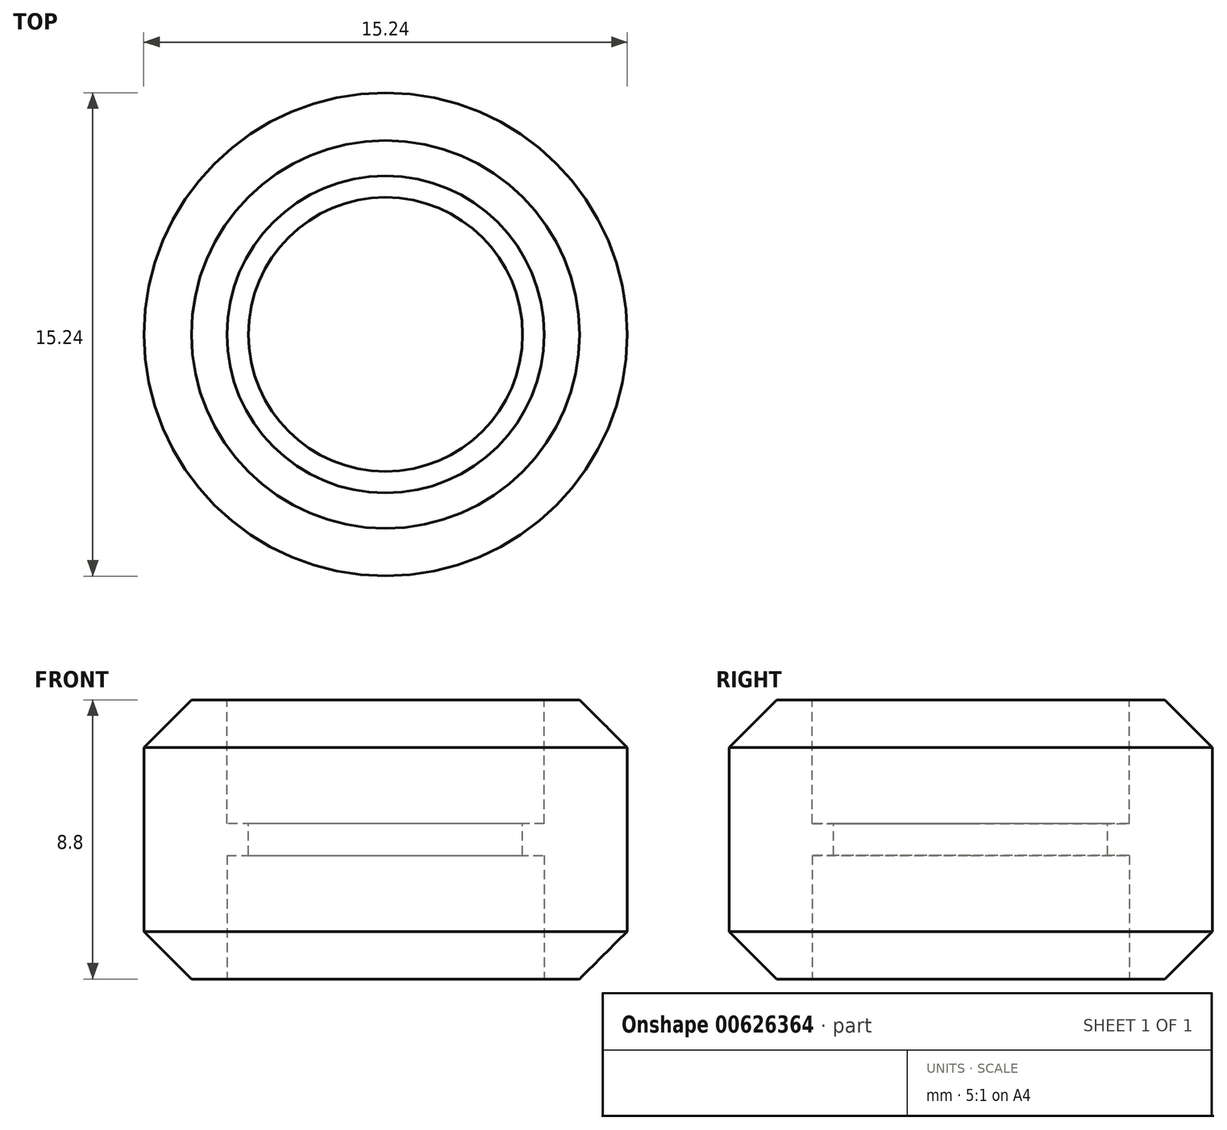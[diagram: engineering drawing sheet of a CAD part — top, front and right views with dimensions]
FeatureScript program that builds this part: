
annotation { "Feature Type Name" : "Feature", "Feature Type Description" : "" }
export const myFeature = defineFeature(function(context is Context, id is Id, definition is map)
    precondition{}
    {
        {
            var Q0;
            Q0=qCreatedBy(makeId("Top.planeOp"),FACE);
            var sketch = newSketch(context, id + "F0", { "sketchPlane" : qUnion([Q0])});
            skCircle(sketch, "E0", {"center": v(0, 0) * mm, "radius": 7.62 * mm});
            skSolve(sketch);
        }
        {
            var Q0;
            Q0 = qSketchRegion(id + "F0", true);
            extrude(context, id + "F1", {"entities" : qUnion([Q0]), "depth" : 8.8 * mm, "offsetDistance" : 25 * mm});
        }
        {
            var Q0;
            Q0=makeQuery(id+"F1.opExtrude","CAP_EDGE",EDGE,{"disambiguationData":[OSD([sQuery(id+"F0.wireOp",EDGE,"E0")])],"isStart":false});
            var Q1;
            Q1=makeQuery(id+"F1.opExtrude","CAP_EDGE",EDGE,{"disambiguationData":[OSD([sQuery(id+"F0.wireOp",EDGE,"E0")])],"isStart":true});
            chamfer(context, id + "F2", {"entities" : qUnion([Q0, Q1]), "width" : 1.5 * mm, "tangentPropagation" : true});
        }
        {
            var Q0;
            Q0=makeQuery(id+"F1.opExtrude","CAP_FACE",FACE,{"disambiguationData":[OSD([sQuery(id+"F0.wireOp",EDGE,"E0")])],"isStart":true});
            var sketch = newSketch(context, id + "F3", { "sketchPlane" : qUnion([Q0])});
            skCircle(sketch, "E1", {"center": v(0, 0) * mm, "radius": 5 * mm});
            skSolve(sketch);
        }
        {
            var Q0;
            Q0 = qSketchRegion(id + "F3", true);
            extrude(context, id + "F4", {"entities" : qUnion([Q0]), "operationType" : NewBodyOperationType.REMOVE, "oppositeDirection" : true, "depth" : 3.9 * mm, "offsetDistance" : 25 * mm});
        }
        {
            var Q0;
            Q0=makeQuery(id+"F1.opExtrude","CAP_FACE",FACE,{"disambiguationData":[OSD([sQuery(id+"F0.wireOp",EDGE,"E0")])],"isStart":false});
            var sketch = newSketch(context, id + "F5", { "sketchPlane" : qUnion([Q0])});
            skCircle(sketch, "E2", {"center": v(0, 0) * mm, "radius": 5 * mm});
            skSolve(sketch);
        }
        {
            var Q0;
            Q0 = qSketchRegion(id + "F5", true);
            extrude(context, id + "F6", {"entities" : qUnion([Q0]), "operationType" : NewBodyOperationType.REMOVE, "oppositeDirection" : true, "depth" : 3.9 * mm, "offsetDistance" : 25 * mm});
        }
        {
            var Q0;
            Q0=makeQuery(id+"F6.boolean.opBoolean","COPY",FACE,{"derivedFrom":makeQuery(id+"F6.opExtrude","CAP_FACE",FACE,{"disambiguationData":[OSD([sQuery(id+"F5.wireOp",EDGE,"E2")])],"isStart":false})});
            var sketch = newSketch(context, id + "F7", { "sketchPlane" : qUnion([Q0])});
            skCircle(sketch, "E3", {"center": v(0, 0) * mm, "radius": 4.32 * mm});
            skSolve(sketch);
        }
        {
            var Q0;
            Q0 = qSketchRegion(id + "F7", true);
            extrude(context, id + "F8", {"entities" : qUnion([Q0]), "operationType" : NewBodyOperationType.REMOVE, "oppositeDirection" : true, "depth" : 25 * mm, "offsetDistance" : 25 * mm});
        }
    });
